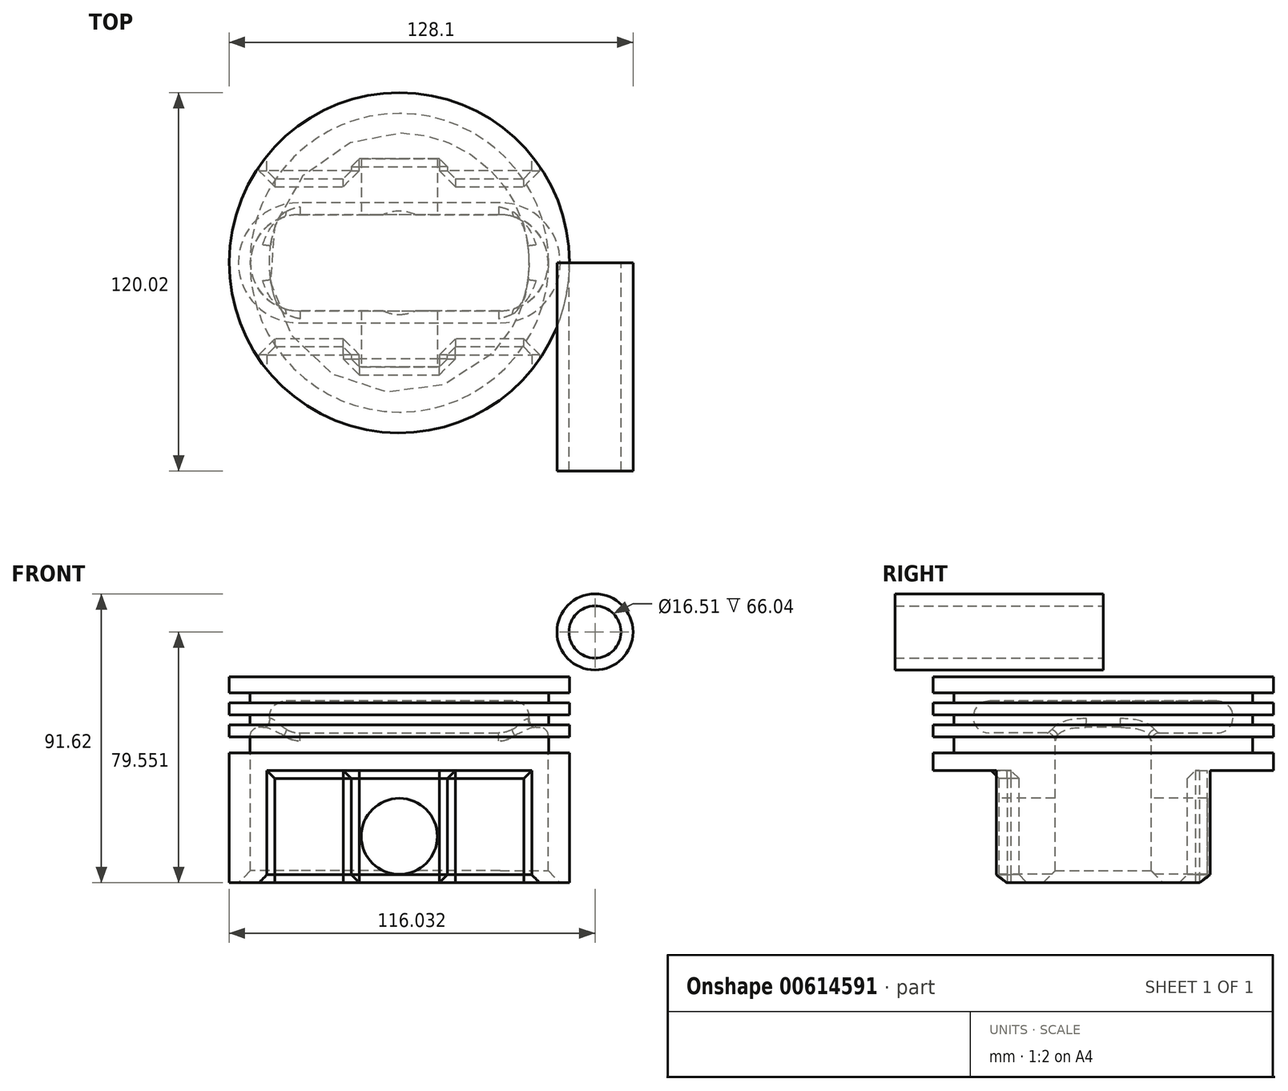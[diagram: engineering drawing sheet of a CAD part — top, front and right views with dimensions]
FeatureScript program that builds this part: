
annotation { "Feature Type Name" : "Feature", "Feature Type Description" : "" }
export const myFeature = defineFeature(function(context is Context, id is Id, definition is map)
    precondition{}
    {
        {
            var Q0;
            Q0=qCreatedBy(makeId("Front.planeOp"),FACE);
            var sketch = newSketch(context, id + "F0", { "sketchPlane" : qUnion([Q0])});
            skLineSegment(sketch, "E0", {"start": v(0, 43.4) * mm, "end": v(-53.98, 43.4) * mm});
            skLineSegment(sketch, "E1", {"start": v(-53.98, 43.4) * mm, "end": v(-53.98, 38.32) * mm});
            skLineSegment(sketch, "E2", {"start": v(-53.98, 38.32) * mm, "end": v(-47.37, 38.32) * mm});
            skLineSegment(sketch, "E3", {"start": v(-47.37, 38.32) * mm, "end": v(-47.37, 35.14) * mm});
            skLineSegment(sketch, "E4", {"start": v(-47.37, 35.14) * mm, "end": v(-53.98, 35.14) * mm});
            skLineSegment(sketch, "E5", {"start": v(-53.98, 35.14) * mm, "end": v(-53.98, 31.33) * mm});
            skLineSegment(sketch, "E6", {"start": v(-53.98, 31.33) * mm, "end": v(-47.37, 31.33) * mm});
            skLineSegment(sketch, "E7", {"start": v(-47.37, 31.33) * mm, "end": v(-47.37, 28.16) * mm});
            skLineSegment(sketch, "E8", {"start": v(-47.37, 28.16) * mm, "end": v(-53.98, 28.16) * mm});
            skLineSegment(sketch, "E9", {"start": v(-53.98, 28.16) * mm, "end": v(-53.98, 24.35) * mm});
            skLineSegment(sketch, "E10", {"start": v(-53.98, 24.35) * mm, "end": v(-47.37, 24.35) * mm});
            skLineSegment(sketch, "E11", {"start": v(-47.37, 24.35) * mm, "end": v(-47.37, 19.27) * mm});
            skLineSegment(sketch, "E12", {"start": v(-47.37, 19.27) * mm, "end": v(-53.98, 19.27) * mm});
            skLineSegment(sketch, "E13", {"start": v(-53.98, 19.27) * mm, "end": v(-53.98, 13.68) * mm});
            skLineSegment(sketch, "E14", {"start": v(-53.98, 13.68) * mm, "end": v(0, 13.68) * mm});
            skLineSegment(sketch, "E15", {"start": v(0, 35.78) * mm, "end": v(-36.13, 35.78) * mm});
            skLineSegment(sketch, "E16", {"start": v(0, 25.62) * mm, "end": v(-36.13, 25.62) * mm});
            skArc(sketch, "E17", {"start": v(-36.13, 35.78) * mm, "mid": v(-41.2, 30.7) * mm, "end": v(-36.13, 25.62) * mm});
            skLineSegment(sketch, "E18", {"start": v(0, 43.4) * mm, "end": v(0, 13.68) * mm});
            skSolve(sketch);
        }
        {
            var Q0;
            {var subQ0=sQuery(id+"F0.wireOp",EDGE,"E0");Q0=makeQuery(id+"F0.imprint","IMPRINT",FACE,{"disambiguationData":[TD([[makeQuery(id+"F0.imprint","IMPRINT",EDGE,{"derivedFrom":subQ0}),1.0]])]});}
            var Q1;
            Q1=sQuery(id+"F0.wireOp",EDGE,"E18");
            revolve(context, id + "F1", {"entities" : qUnion([Q0]), "axis" : qUnion([Q1]), "revolveType" : RevolveType.FULL});
        }
        {
            var Q0;
            Q0=makeQuery(id+"F1.opRevolve","SWEPT_FACE",FACE,{"disambiguationData":[OSD([sQuery(id+"F0.wireOp",EDGE,"E14")])]});
            var sketch = newSketch(context, id + "F2", { "sketchPlane" : qUnion([Q0])});
            skLineSegment(sketch, "E19", {"start": v(0, 15.24) * mm, "end": v(-31.97, 15.24) * mm});
            skLineSegment(sketch, "E20", {"start": v(-15.24, 26.67) * mm, "end": v(-42, 26.67) * mm});
            skLineSegment(sketch, "E21", {"start": v(-42, 26.67) * mm, "end": v(-42, 33.9) * mm});
            skLineSegment(sketch, "E22.MirrorCS", {"start": v(15.24, 26.67) * mm, "end": v(42, 26.67) * mm});
            skLineSegment(sketch, "E23.MirrorCS", {"start": v(0, 15.24) * mm, "end": v(31.97, 15.24) * mm});
            skLineSegment(sketch, "E24.MirrorCS", {"start": v(42, 26.67) * mm, "end": v(42, 33.9) * mm});
            skLineSegment(sketch, "E25.MirrorCS", {"start": v(0, -15.24) * mm, "end": v(-31.97, -15.24) * mm});
            skLineSegment(sketch, "E26.MirrorCS", {"start": v(0, -15.24) * mm, "end": v(31.97, -15.24) * mm});
            skLineSegment(sketch, "E27.MirrorCS", {"start": v(15.24, -26.67) * mm, "end": v(42, -26.67) * mm});
            skLineSegment(sketch, "E28.MirrorCS", {"start": v(-15.24, -26.67) * mm, "end": v(-42, -26.67) * mm});
            skLineSegment(sketch, "E29.MirrorCS", {"start": v(-42, -26.67) * mm, "end": v(-42, -33.9) * mm});
            skLineSegment(sketch, "E30.MirrorCS", {"start": v(42, -26.67) * mm, "end": v(42, -33.9) * mm});
            skArc(sketch, "E31", {"start": v(-31.97, 15.24) * mm, "mid": v(-47.21, 0) * mm, "end": v(-31.97, -15.24) * mm});
            skArc(sketch, "E32", {"start": v(31.97, 15.24) * mm, "mid": v(47.21, 0) * mm, "end": v(31.97, -15.24) * mm});
            skLineSegment(sketch, "E33", {"start": v(0, 33.02) * mm, "end": v(-15.24, 33.02) * mm});
            skLineSegment(sketch, "E34", {"start": v(-15.24, 33.02) * mm, "end": v(-15.24, 26.67) * mm});
            skLineSegment(sketch, "E35.MirrorCS", {"start": v(0, 33.02) * mm, "end": v(15.24, 33.02) * mm});
            skLineSegment(sketch, "E36.MirrorCS", {"start": v(15.24, 33.02) * mm, "end": v(15.24, 26.67) * mm});
            skLineSegment(sketch, "E37.MirrorCS", {"start": v(0, -33.02) * mm, "end": v(15.24, -33.02) * mm});
            skLineSegment(sketch, "E38.MirrorCS", {"start": v(15.24, -33.02) * mm, "end": v(15.24, -26.67) * mm});
            skLineSegment(sketch, "E39.MirrorCS", {"start": v(0, -33.02) * mm, "end": v(-15.24, -33.02) * mm});
            skLineSegment(sketch, "E40.MirrorCS", {"start": v(-15.24, -33.02) * mm, "end": v(-15.24, -26.67) * mm});
            skPoint(sketch, "E41.orphan", {"position": v(0, 26.67) * mm});
            skPoint(sketch, "E42.orphan", {"position": v(0, -26.67) * mm});
            skSolve(sketch);
        }
        {
            var Q0;
            Q0=makeQuery(id+"F2.imprint","IMPRINT",FACE,{"disambiguationData":[TD([[makeQuery(id+"F2.imprint","IMPRINT",EDGE,{"derivedFrom":sQuery(id+"F2.wireOp",EDGE,"E19")}),-1.0]])]});
            extrude(context, id + "F3", {"entities" : qUnion([Q0]), "operationType" : NewBodyOperationType.ADD, "depth" : 35.56 * mm, "offsetDistance" : 25.4 * mm});
        }
        {
            var Q0;
            Q0=makeQuery(id+"F3.opExtrude","SWEPT_FACE",FACE,{"disambiguationData":[OSD([sQuery(id+"F2.wireOp",EDGE,"E33"),sQuery(id+"F2.wireOp",EDGE,"E35.MirrorCS")])]});
            var sketch = newSketch(context, id + "F4", { "sketchPlane" : qUnion([Q0])});
            skCircle(sketch, "E43", {"center": v(0, -7.15) * mm, "radius": 12.07 * mm});
            skSolve(sketch);
        }
        {
            var Q0;
            Q0=makeQuery(id+"F4.imprint","IMPRINT",FACE,{"disambiguationData":[TD([[makeQuery(id+"F4.imprint","IMPRINT",EDGE,{"derivedFrom":sQuery(id+"F4.wireOp",EDGE,"E43")}),1.0]])]});
            extrude(context, id + "F5", {"entities" : qUnion([Q0]), "operationType" : NewBodyOperationType.REMOVE, "oppositeDirection" : true, "depth" : 98.8 * mm, "offsetDistance" : 25.4 * mm});
        }
        {
            var Q0;
            Q0=makeQuery(id+"F3.opExtrude","CAP_EDGE",EDGE,{"disambiguationData":[OSD([sQuery(id+"F2.wireOp",EDGE,"E31")])],"isStart":false});
            chamfer(context, id + "F6", {"entities" : qUnion([Q0]), "width" : 3.8 * mm, "tangentPropagation" : true});
        }
        {
            var Q0;
            Q0=makeQuery(id+"F3.boolean.opBoolean","SPLIT",FACE,{"disambiguationData":[TD([makeQuery(id+"F3.opExtrude","SWEPT_FACE",FACE,{"disambiguationData":[OSD([sQuery(id+"F2.wireOp",EDGE,"E31")])]})])],"derivedFrom":makeQuery(id+"F1.opRevolve","SWEPT_FACE",FACE,{"disambiguationData":[OSD([sQuery(id+"F0.wireOp",EDGE,"E14")])]})});
            extrude(context, id + "F7", {"entities" : qUnion([Q0]), "operationType" : NewBodyOperationType.REMOVE, "oppositeDirection" : true, "depth" : 13.72 * mm, "offsetDistance" : 25.4 * mm});
        }
        {
            var Q0;
            {var subQ0=sQuery(id+"F2.wireOp",EDGE,"E31");Q0=makeQuery(id+"F7.boolean.opBoolean","COPY",FACE,{"disambiguationData":[TD([makeQuery(id+"F3.opExtrude","SWEPT_FACE",FACE,{"disambiguationData":[OSD([subQ0])]})])],"derivedFrom":makeQuery(id+"F7.opExtrude","CAP_FACE",FACE,{"disambiguationData":[OSD([sQuery(id+"F0.wireOp",EDGE,"E14")])],"isStart":false})});}
            var Q1;
            Q1=makeQuery(id+"F7.boolean.opBoolean","INTERSECT",EDGE,{"derivedFrom":[makeQuery(id+"F1.opRevolve","SWEPT_FACE",FACE,{"disambiguationData":[OSD([sQuery(id+"F0.wireOp",EDGE,"E16")])]}),makeQuery(id+"F7.opExtrude","SWEPT_FACE",FACE,{"disambiguationData":[OSD([sQuery(id+"F2.wireOp",EDGE,"E19"),sQuery(id+"F2.wireOp",EDGE,"E23.MirrorCS")])]})]});
            var Q2;
            {var subQ0=sQuery(id+"F2.wireOp",EDGE,"E32");Q2=makeQuery(id+"F7.boolean.opBoolean","COPY",FACE,{"disambiguationData":[TD([makeQuery(id+"F3.opExtrude","SWEPT_FACE",FACE,{"disambiguationData":[OSD([subQ0])]})])],"derivedFrom":makeQuery(id+"F7.opExtrude","CAP_FACE",FACE,{"disambiguationData":[OSD([sQuery(id+"F0.wireOp",EDGE,"E14")])],"isStart":false})});}
            var Q3;
            Q3=makeQuery(id+"F7.boolean.opBoolean","INTERSECT",EDGE,{"derivedFrom":[makeQuery(id+"F1.opRevolve","SWEPT_FACE",FACE,{"disambiguationData":[OSD([sQuery(id+"F0.wireOp",EDGE,"E16")])]}),makeQuery(id+"F7.opExtrude","SWEPT_FACE",FACE,{"disambiguationData":[OSD([sQuery(id+"F2.wireOp",EDGE,"E25.MirrorCS"),sQuery(id+"F2.wireOp",EDGE,"E26.MirrorCS")])]})]});
            fillet(context, id + "F8", {"entities" : qUnion([Q0, Q1, Q2, Q3]), "radius" : 2.54 * mm, "tangentPropagation" : true, "allowEdgeOverflow" : false});
        }
        {
            var Q0;
            Q0=makeQuery(id+"F3.opExtrude","SWEPT_EDGE",EDGE,{"disambiguationData":[OSD([sQuery(id+"F2.wireOp",EDGE,"E20"),sQuery(id+"F2.wireOp",EDGE,"E21")])]});
            var Q1;
            Q1=makeQuery(id+"F3.opExtrude","SWEPT_EDGE",EDGE,{"disambiguationData":[OSD([sQuery(id+"F2.wireOp",EDGE,"E22.MirrorCS"),sQuery(id+"F2.wireOp",EDGE,"E24.MirrorCS")])]});
            var Q2;
            Q2=makeQuery(id+"F3.opExtrude","CAP_EDGE",EDGE,{"disambiguationData":[OSD([sQuery(id+"F2.wireOp",EDGE,"E22.MirrorCS")])],"isStart":true});
            var Q3;
            Q3=makeQuery(id+"F3.opExtrude","SWEPT_FACE",FACE,{"disambiguationData":[OSD([sQuery(id+"F2.wireOp",EDGE,"E22.MirrorCS")])]});
            var Q4;
            Q4=makeQuery(id+"F3.opExtrude","SWEPT_FACE",FACE,{"disambiguationData":[OSD([sQuery(id+"F2.wireOp",EDGE,"E20")])]});
            var Q5;
            Q5=makeQuery(id+"F3.opExtrude","CAP_EDGE",EDGE,{"disambiguationData":[OSD([sQuery(id+"F2.wireOp",EDGE,"E33"),sQuery(id+"F2.wireOp",EDGE,"E35.MirrorCS")])],"isStart":false});
            var Q6;
            Q6=makeQuery(id+"F3.opExtrude","SWEPT_EDGE",EDGE,{"disambiguationData":[OSD([sQuery(id+"F2.wireOp",EDGE,"E33"),sQuery(id+"F2.wireOp",EDGE,"E34")])]});
            var Q7;
            Q7=makeQuery(id+"F3.opExtrude","SWEPT_EDGE",EDGE,{"disambiguationData":[OSD([sQuery(id+"F2.wireOp",EDGE,"E35.MirrorCS"),sQuery(id+"F2.wireOp",EDGE,"E36.MirrorCS")])]});
            var Q8;
            Q8=makeQuery(id+"F3.opExtrude","CAP_EDGE",EDGE,{"disambiguationData":[OSD([sQuery(id+"F2.wireOp",EDGE,"E33"),sQuery(id+"F2.wireOp",EDGE,"E35.MirrorCS")])],"isStart":true});
            var Q9;
            Q9=makeQuery(id+"F3.opExtrude","SWEPT_FACE",FACE,{"disambiguationData":[OSD([sQuery(id+"F2.wireOp",EDGE,"E27.MirrorCS")])]});
            var Q10;
            Q10=makeQuery(id+"F3.opExtrude","SWEPT_FACE",FACE,{"disambiguationData":[OSD([sQuery(id+"F2.wireOp",EDGE,"E28.MirrorCS")])]});
            var Q11;
            Q11=makeQuery(id+"F3.opExtrude","CAP_EDGE",EDGE,{"disambiguationData":[OSD([sQuery(id+"F2.wireOp",EDGE,"E37.MirrorCS"),sQuery(id+"F2.wireOp",EDGE,"E39.MirrorCS")])],"isStart":false});
            var Q12;
            Q12=makeQuery(id+"F3.opExtrude","SWEPT_EDGE",EDGE,{"disambiguationData":[OSD([sQuery(id+"F2.wireOp",EDGE,"E39.MirrorCS"),sQuery(id+"F2.wireOp",EDGE,"E40.MirrorCS")])]});
            var Q13;
            Q13=makeQuery(id+"F3.opExtrude","CAP_EDGE",EDGE,{"disambiguationData":[OSD([sQuery(id+"F2.wireOp",EDGE,"E37.MirrorCS"),sQuery(id+"F2.wireOp",EDGE,"E39.MirrorCS")])],"isStart":true});
            var Q14;
            Q14=makeQuery(id+"F3.opExtrude","CAP_EDGE",EDGE,{"disambiguationData":[OSD([sQuery(id+"F2.wireOp",EDGE,"E40.MirrorCS")])],"isStart":true});
            var Q15;
            Q15=makeQuery(id+"F3.opExtrude","SWEPT_EDGE",EDGE,{"disambiguationData":[OSD([sQuery(id+"F2.wireOp",EDGE,"E37.MirrorCS"),sQuery(id+"F2.wireOp",EDGE,"E38.MirrorCS")])]});
            var Q16;
            Q16=makeQuery(id+"F3.opExtrude","CAP_EDGE",EDGE,{"disambiguationData":[OSD([sQuery(id+"F2.wireOp",EDGE,"E38.MirrorCS")])],"isStart":true});
            chamfer(context, id + "F9", {"entities" : qUnion([Q0, Q1, Q2, Q3, Q4, Q5, Q6, Q7, Q8, Q9, Q10, Q11, Q12, Q13, Q14, Q15, Q16]), "width" : 2.54 * mm, "tangentPropagation" : true});
        }
        {
            var Q0;
            Q0=qCreatedBy(makeId("Front.planeOp"),FACE);
            var sketch = newSketch(context, id + "F10", { "sketchPlane" : qUnion([Q0])});
            skCircle(sketch, "E44", {"center": v(62.05, 57.67) * mm, "radius": 12.07 * mm});
            skCircle(sketch, "E45.0", {"center": v(62.05, 57.67) * mm, "radius": 8.26 * mm});
            skSolve(sketch);
        }
        {
            var Q0;
            Q0=makeQuery(id+"F10.imprint","IMPRINT",FACE,{"disambiguationData":[TD([[makeQuery(id+"F10.imprint","IMPRINT",EDGE,{"derivedFrom":sQuery(id+"F10.wireOp",EDGE,"E44")}),1.0]])]});
            extrude(context, id + "F11", {"entities" : qUnion([Q0]), "depth" : 66.04 * mm, "offsetDistance" : 25.4 * mm});
        }
    });
